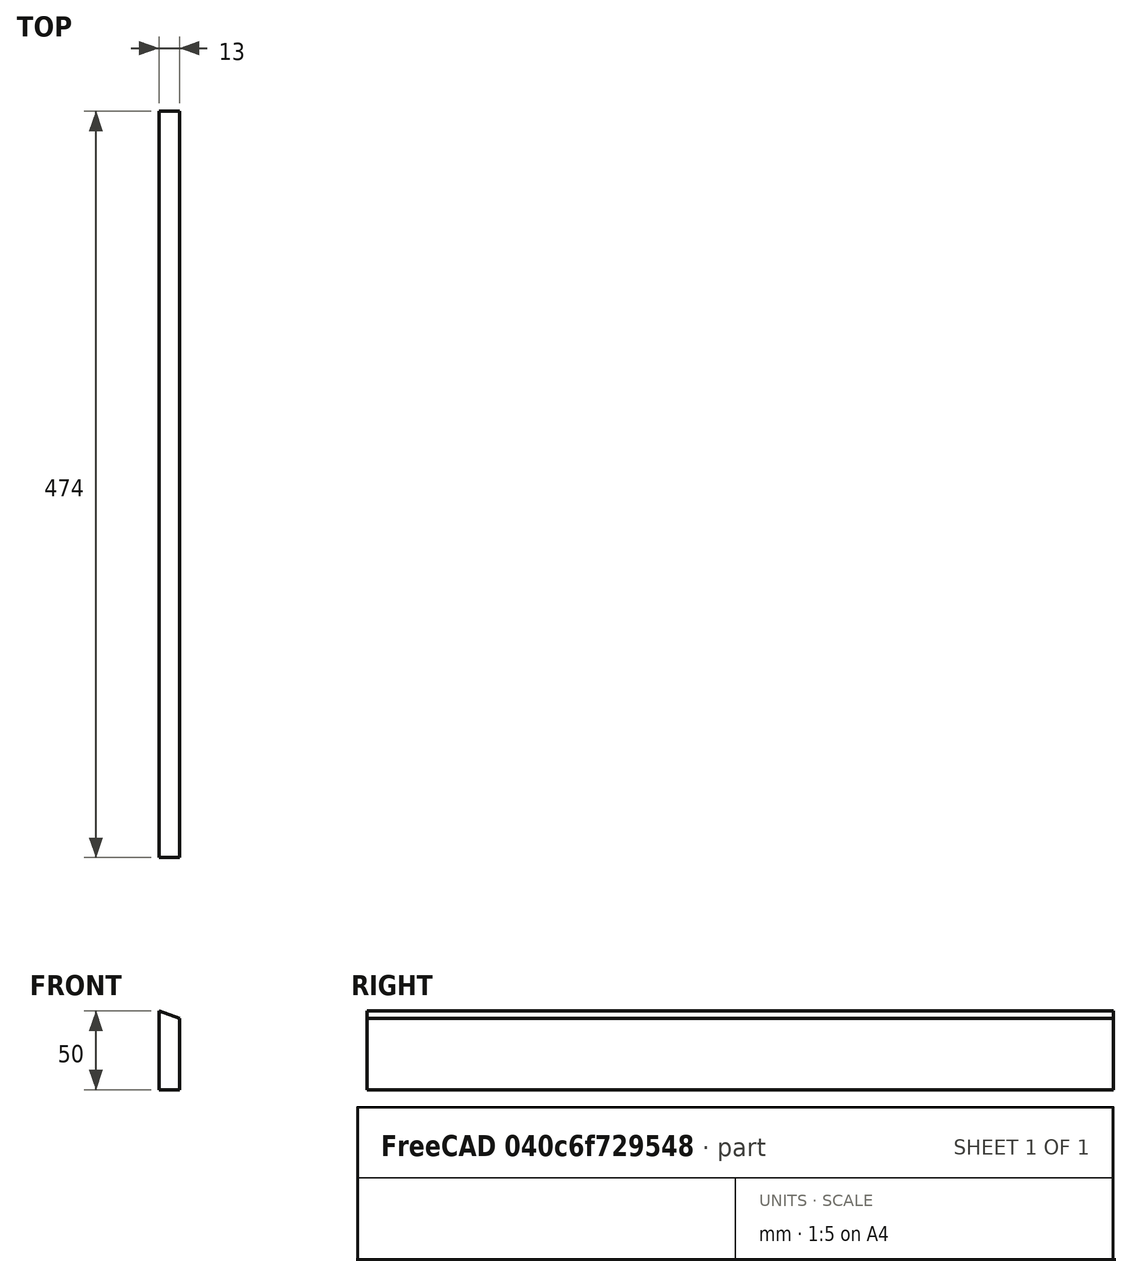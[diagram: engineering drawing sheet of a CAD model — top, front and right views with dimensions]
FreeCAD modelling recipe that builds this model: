
FCSTD DOCUMENT  (FreeCAD 0.18R14555 (Git shallow))
Label: 4000_Body_front_base_YZ
License: All rights reserved
LicenseURL: http://en.wikipedia.org/wiki/All_rights_reserved
objects: Spreadsheet::Sheet×1, Sketcher::SketchObject×1, PartDesign::Pad×1, PartDesign::Body×1
note: 4 computed .brp shape members not serialized (recipe doc carries the construction recipe); baked Part::Feature solids carry a one-line shape summary decoded from their .brp

FEATURE [Spreadsheet::Sheet] Spreadsheet  label="xls"
  cells = B5=BODY FRONT; E5=nominal size; B6=Board Thickness; C6(thickness)=13; D6=xls.thickness; B7=Horizontal Y; C7(width)==+E7 - 2 * C6; D7=xls.width; E7=500; B8=X=; C8(height)=50; D8=xls.height; B9=Angle Y; C9(tilt)=90; D9=xls.tilt
FEATURE [Sketcher::SketchObject] Sketch
  MapMode = 5
  Placement = pos=(0,0,0) rot=(1,0,0;1.5708rad)
  Support = -> [XZ_Plane]
  expr: Constraints[9] = xls.height
  expr: Constraints[6] = xls.tilt
  expr: Constraints[5] = xls.thickness
  sketch-geometry (4):
    g0: LineSegment StartX=13 StartY=-1.4345e-12 StartZ=0 EndX=13 EndY=45.2684 EndZ=0
    g1: LineSegment StartX=13 StartY=45.2684 StartZ=0 EndX=8.5603e-12 EndY=50 EndZ=0
    g2: LineSegment StartX=8.5603e-12 StartY=50 StartZ=0 EndX=0 EndY=0 EndZ=0
    g3: LineSegment StartX=0 StartY=0 StartZ=0 EndX=13 EndY=-1.4345e-12 EndZ=0
  constraints (11):
    c: Coincident(g0,g1)
    c: Coincident(g1,g2)
    c: Coincident(g2,g3)
    c: Parallel(g0,g2)
    c: Perpendicular(g0,g3)
    c: Distance(g3) = 13
    c: Angle(g-1,g0) = 1.5708
    c: Coincident(g0,g3)
    c: Coincident(g-1,g2)
    c: DistanceY(g2,g2) = 50
    c: Angle(g1,g0) = 1.91986
FEATURE [PartDesign::Pad] Pad
  Length = 474
  Length2 = 100
  Placement = pos=(0,0,0) rot=(1,0,0;1.5708rad)
  Profile = -> Sketch
  Reversed = true
  Type = 0
  expr: Length = xls.width
FEATURE [PartDesign::Body] Body
  Group = -> [Sketch,Pad]
  Origin = -> Origin
  Tip = -> Pad
